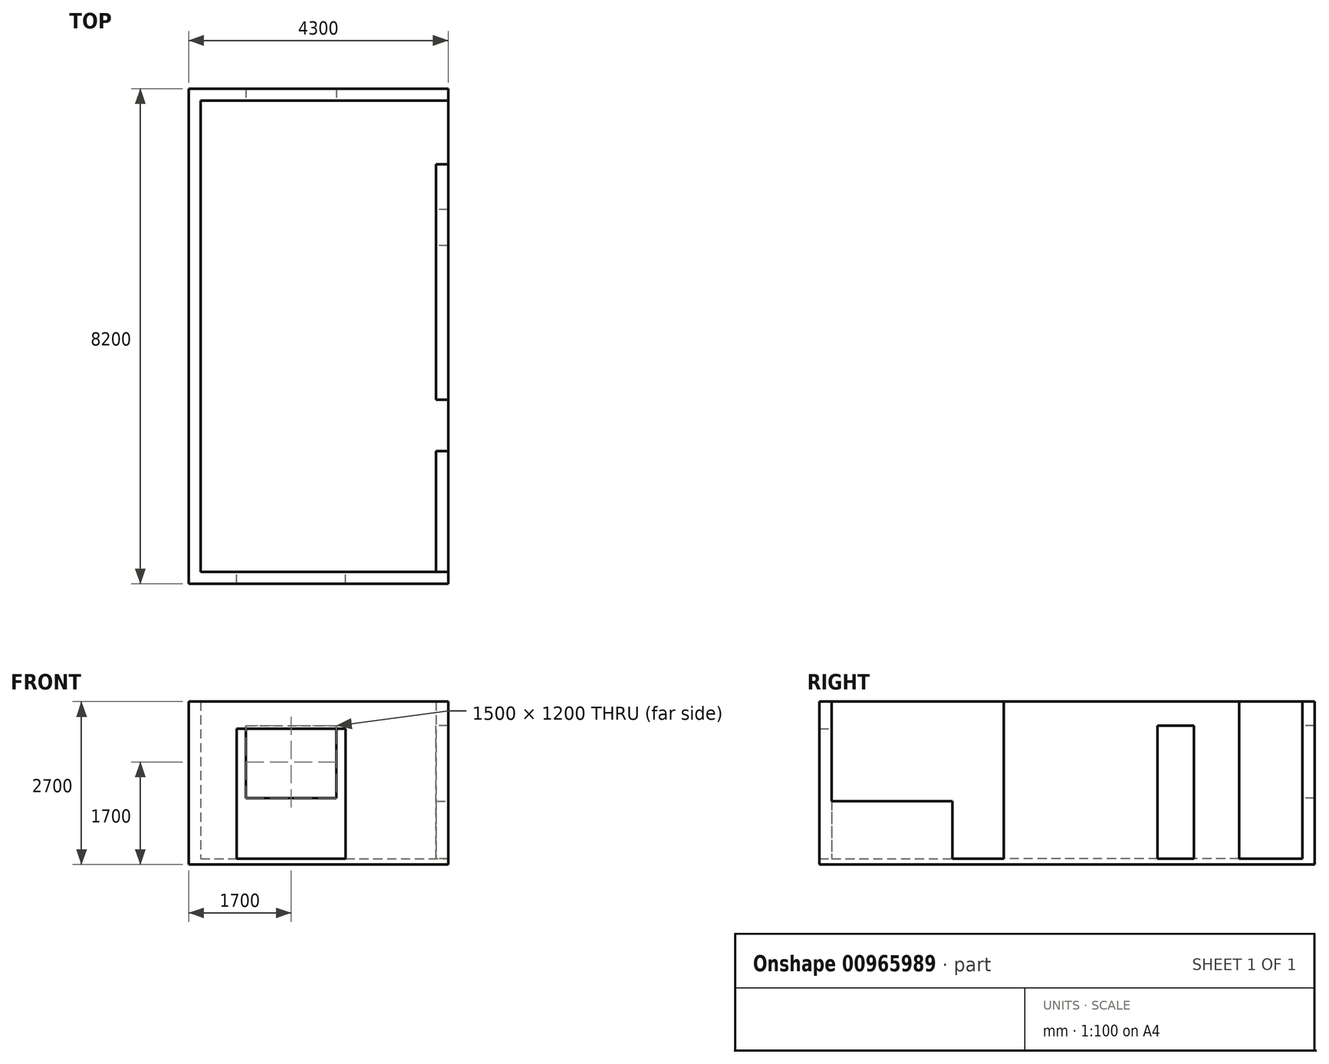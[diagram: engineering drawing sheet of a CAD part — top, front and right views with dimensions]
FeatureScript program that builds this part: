
annotation { "Feature Type Name" : "Feature", "Feature Type Description" : "" }
export const myFeature = defineFeature(function(context is Context, id is Id, definition is map)
    precondition{}
    {
        {
            var Q0;
            Q0=qCreatedBy(makeId("Top.planeOp"),FACE);
            var sketch = newSketch(context, id + "F0", { "sketchPlane" : qUnion([Q0])});
            skLineSegment(sketch, "E0.bottom", {"start": v(-1950, 3900) * mm, "end": v(1950, 3900) * mm});
            skLineSegment(sketch, "E0.top", {"start": v(-1950, -3900) * mm, "end": v(1950, -3900) * mm});
            skLineSegment(sketch, "E0.left", {"start": v(-1950, 3900) * mm, "end": v(-1950, -3900) * mm});
            skLineSegment(sketch, "E0.right", {"start": v(1950, 3900) * mm, "end": v(1950, -3900) * mm});
            skLineSegment(sketch, "E1", {"start": v(-1950, 3900) * mm, "end": v(1950, -3900) * mm, "construction": true});
            skSolve(sketch);
        }
        {
            var Q0;
            Q0 = qSketchRegion(id + "F0", true);
            extrude(context, id + "F1", {"entities" : qUnion([Q0]), "oppositeDirection" : true, "depth" : 100 * mm, "offsetDistance" : 25 * mm});
        }
        {
            var Q0;
            Q0=qCreatedBy(makeId("Top.planeOp"),FACE);
            var sketch = newSketch(context, id + "F2", { "sketchPlane" : qUnion([Q0])});
            skLineSegment(sketch, "E2.bottom", {"start": v(-1950, 3900) * mm, "end": v(1950, 3900) * mm});
            skLineSegment(sketch, "E2.top", {"start": v(-1950, -3900) * mm, "end": v(1950, -3900) * mm});
            skLineSegment(sketch, "E2.left", {"start": v(-1950, 3900) * mm, "end": v(-1950, -3900) * mm});
            skLineSegment(sketch, "E2.right", {"start": v(1950, 3900) * mm, "end": v(1950, -3900) * mm});
            skLineSegment(sketch, "E3.0", {"start": v(-2150, 4100) * mm, "end": v(-2150, -4100) * mm});
            skLineSegment(sketch, "E3.1", {"start": v(-2150, 4100) * mm, "end": v(2150, 4100) * mm});
            skLineSegment(sketch, "E3.2", {"start": v(2150, 4100) * mm, "end": v(2150, -4100) * mm});
            skLineSegment(sketch, "E3.3", {"start": v(-2150, -4100) * mm, "end": v(2150, -4100) * mm});
            skSolve(sketch);
        }
        {
            var Q0;
            Q0 = qSketchRegion(id + "F2", true);
            var Q1;
            Q1=makeQuery(id+"F1.opExtrude","CAP_FACE",FACE,{"disambiguationData":[OSD([sQuery(id+"F0.wireOp",EDGE,"E0.bottom"),sQuery(id+"F0.wireOp",EDGE,"E0.top"),sQuery(id+"F0.wireOp",EDGE,"E0.left"),sQuery(id+"F0.wireOp",EDGE,"E0.right")])],"isStart":false});
            extrude(context, id + "F3", {"entities" : qUnion([Q0]), "operationType" : NewBodyOperationType.ADD, "depth" : 2600 * mm, "offsetDistance" : 25 * mm, "hasSecondDirection" : true, "secondDirectionBound" : SecondDirectionBoundingType.UP_TO_SURFACE, "secondDirectionOppositeDirection" : true, "secondDirectionDepth" : 25 * mm, "secondDirectionBoundEntityFace" : qUnion([Q1])});
        }
        {
            var Q0;
            Q0=makeQuery(id+"F1.opExtrude","CAP_FACE",FACE,{"disambiguationData":[OSD([sQuery(id+"F0.wireOp",EDGE,"E0.bottom"),sQuery(id+"F0.wireOp",EDGE,"E0.top"),sQuery(id+"F0.wireOp",EDGE,"E0.left"),sQuery(id+"F0.wireOp",EDGE,"E0.right")])],"isStart":true});
            var sketch = newSketch(context, id + "F4", { "sketchPlane" : qUnion([Q0])});
            skLineSegment(sketch, "E4.bottom", {"start": v(1950, 3900) * mm, "end": v(2150, 3900) * mm});
            skLineSegment(sketch, "E4.top", {"start": v(1950, 2850) * mm, "end": v(2150, 2850) * mm});
            skLineSegment(sketch, "E4.left", {"start": v(1950, 3900) * mm, "end": v(1950, 2850) * mm});
            skLineSegment(sketch, "E4.right", {"start": v(2150, 3900) * mm, "end": v(2150, 2850) * mm});
            skLineSegment(sketch, "E5.bottom", {"start": v(1950, -3900) * mm, "end": v(2150, -3900) * mm});
            skLineSegment(sketch, "E5.top", {"start": v(1950, -1050) * mm, "end": v(2150, -1050) * mm});
            skLineSegment(sketch, "E5.left", {"start": v(1950, -3900) * mm, "end": v(1950, -1050) * mm});
            skLineSegment(sketch, "E5.right", {"start": v(2150, -3900) * mm, "end": v(2150, -1050) * mm});
            skSolve(sketch);
        }
        {
            var Q0;
            Q0 = qSketchRegion(id + "F4", true);
            extrude(context, id + "F5", {"entities" : qUnion([Q0]), "operationType" : NewBodyOperationType.REMOVE, "endBound" : BoundingType.THROUGH_ALL, "depth" : 25 * mm, "offsetDistance" : 25 * mm});
        }
        {
            var Q0;
            Q0=makeQuery(id+"F5.boolean.opBoolean","MERGE",FACE,{"derivedFrom":[makeQuery(id+"F3.opExtrude","SWEPT_FACE",FACE,{"disambiguationData":[OSD([sQuery(id+"F2.wireOp",EDGE,"E2.bottom")])]})],"fromTools":[makeQuery(id+"F5.opExtrude","SWEPT_FACE",FACE,{"disambiguationData":[OSD([sQuery(id+"F4.wireOp",EDGE,"E4.bottom")])]})]});
            var sketch = newSketch(context, id + "F6", { "sketchPlane" : qUnion([Q0])});
            skLineSegment(sketch, "E6.bottom", {"start": v(-1200, 2200) * mm, "end": v(300, 2200) * mm});
            skLineSegment(sketch, "E6.top", {"start": v(-1200, 1000) * mm, "end": v(300, 1000) * mm});
            skLineSegment(sketch, "E6.left", {"start": v(-1200, 2200) * mm, "end": v(-1200, 1000) * mm});
            skLineSegment(sketch, "E6.right", {"start": v(300, 2200) * mm, "end": v(300, 1000) * mm});
            skSolve(sketch);
        }
        {
            var Q0;
            Q0 = qSketchRegion(id + "F6", true);
            extrude(context, id + "F7", {"entities" : qUnion([Q0]), "operationType" : NewBodyOperationType.REMOVE, "endBound" : BoundingType.THROUGH_ALL, "oppositeDirection" : true, "depth" : 25 * mm, "offsetDistance" : 25 * mm});
        }
        {
            var Q0;
            Q0=makeQuery(id+"F5.boolean.opBoolean","MERGE",FACE,{"derivedFrom":[makeQuery(id+"F3.opExtrude","SWEPT_FACE",FACE,{"disambiguationData":[OSD([sQuery(id+"F2.wireOp",EDGE,"E2.top")])]})],"fromTools":[makeQuery(id+"F5.opExtrude","SWEPT_FACE",FACE,{"disambiguationData":[OSD([sQuery(id+"F4.wireOp",EDGE,"E5.bottom")])]})]});
            var sketch = newSketch(context, id + "F8", { "sketchPlane" : qUnion([Q0])});
            skLineSegment(sketch, "E7.bottom", {"start": v(1350, 0) * mm, "end": v(-450, 0) * mm});
            skLineSegment(sketch, "E7.top", {"start": v(1350, 2150) * mm, "end": v(-450, 2150) * mm});
            skLineSegment(sketch, "E7.left", {"start": v(1350, 0) * mm, "end": v(1350, 2150) * mm});
            skLineSegment(sketch, "E7.right", {"start": v(-450, 0) * mm, "end": v(-450, 2150) * mm});
            skSolve(sketch);
        }
        {
            var Q0;
            Q0 = qSketchRegion(id + "F8", true);
            extrude(context, id + "F9", {"entities" : qUnion([Q0]), "operationType" : NewBodyOperationType.REMOVE, "endBound" : BoundingType.THROUGH_ALL, "oppositeDirection" : true, "depth" : 25 * mm, "offsetDistance" : 25 * mm});
        }
        {
            var Q0;
            Q0=makeQuery(id+"F3.opExtrude","SWEPT_FACE",FACE,{"disambiguationData":[OSD([sQuery(id+"F2.wireOp",EDGE,"E2.right")])]});
            var sketch = newSketch(context, id + "F10", { "sketchPlane" : qUnion([Q0])});
            skLineSegment(sketch, "E8.bottom", {"start": v(-2100, 0) * mm, "end": v(-1500, 0) * mm});
            skLineSegment(sketch, "E8.top", {"start": v(-2100, 2200) * mm, "end": v(-1500, 2200) * mm});
            skLineSegment(sketch, "E8.left", {"start": v(-2100, 0) * mm, "end": v(-2100, 2200) * mm});
            skLineSegment(sketch, "E8.right", {"start": v(-1500, 0) * mm, "end": v(-1500, 2200) * mm});
            skSolve(sketch);
        }
        {
            var Q0;
            Q0 = qSketchRegion(id + "F10", true);
            extrude(context, id + "F11", {"entities" : qUnion([Q0]), "operationType" : NewBodyOperationType.REMOVE, "endBound" : BoundingType.THROUGH_ALL, "oppositeDirection" : true, "depth" : 25 * mm, "offsetDistance" : 25 * mm});
        }
        {
            var Q0;
            Q0=makeQuery(id+"F11.boolean.opBoolean","MERGE",FACE,{"derivedFrom":[makeQuery(id+"F9.boolean.opBoolean","MERGE",FACE,{"derivedFrom":[makeQuery(id+"F5.boolean.opBoolean","MERGE",FACE,{"derivedFrom":[makeQuery(id+"F1.opExtrude","CAP_FACE",FACE,{"disambiguationData":[OSD([sQuery(id+"F0.wireOp",EDGE,"E0.bottom"),sQuery(id+"F0.wireOp",EDGE,"E0.top"),sQuery(id+"F0.wireOp",EDGE,"E0.left"),sQuery(id+"F0.wireOp",EDGE,"E0.right")])],"isStart":true})],"fromTools":[makeQuery(id+"F5.opExtrude","CAP_FACE",FACE,{"disambiguationData":[OSD([sQuery(id+"F4.wireOp",EDGE,"E4.bottom"),sQuery(id+"F4.wireOp",EDGE,"E4.top"),sQuery(id+"F4.wireOp",EDGE,"E4.left"),sQuery(id+"F4.wireOp",EDGE,"E4.right")])],"isStart":true}),makeQuery(id+"F5.opExtrude","CAP_FACE",FACE,{"disambiguationData":[OSD([sQuery(id+"F4.wireOp",EDGE,"E5.bottom"),sQuery(id+"F4.wireOp",EDGE,"E5.top"),sQuery(id+"F4.wireOp",EDGE,"E5.left"),sQuery(id+"F4.wireOp",EDGE,"E5.right")])],"isStart":true})]})],"fromTools":[makeQuery(id+"F9.opExtrude","SWEPT_FACE",FACE,{"disambiguationData":[OSD([sQuery(id+"F8.wireOp",EDGE,"E7.bottom")])]})]})],"fromTools":[makeQuery(id+"F11.opExtrude","SWEPT_FACE",FACE,{"disambiguationData":[OSD([sQuery(id+"F10.wireOp",EDGE,"E8.bottom")])]})]});
            var sketch = newSketch(context, id + "F12", { "sketchPlane" : qUnion([Q0])});
            skLineSegment(sketch, "E9.bottom", {"start": v(2150, -3900) * mm, "end": v(1950, -3900) * mm});
            skLineSegment(sketch, "E9.top", {"start": v(2150, -1900) * mm, "end": v(1950, -1900) * mm});
            skLineSegment(sketch, "E9.left", {"start": v(2150, -3900) * mm, "end": v(2150, -1900) * mm});
            skLineSegment(sketch, "E9.right", {"start": v(1950, -3900) * mm, "end": v(1950, -1900) * mm});
            skSolve(sketch);
        }
        {
            var Q0;
            Q0 = qSketchRegion(id + "F12", true);
            extrude(context, id + "F13", {"entities" : qUnion([Q0]), "operationType" : NewBodyOperationType.ADD, "depth" : 950 * mm, "offsetDistance" : 25 * mm});
        }
    });
